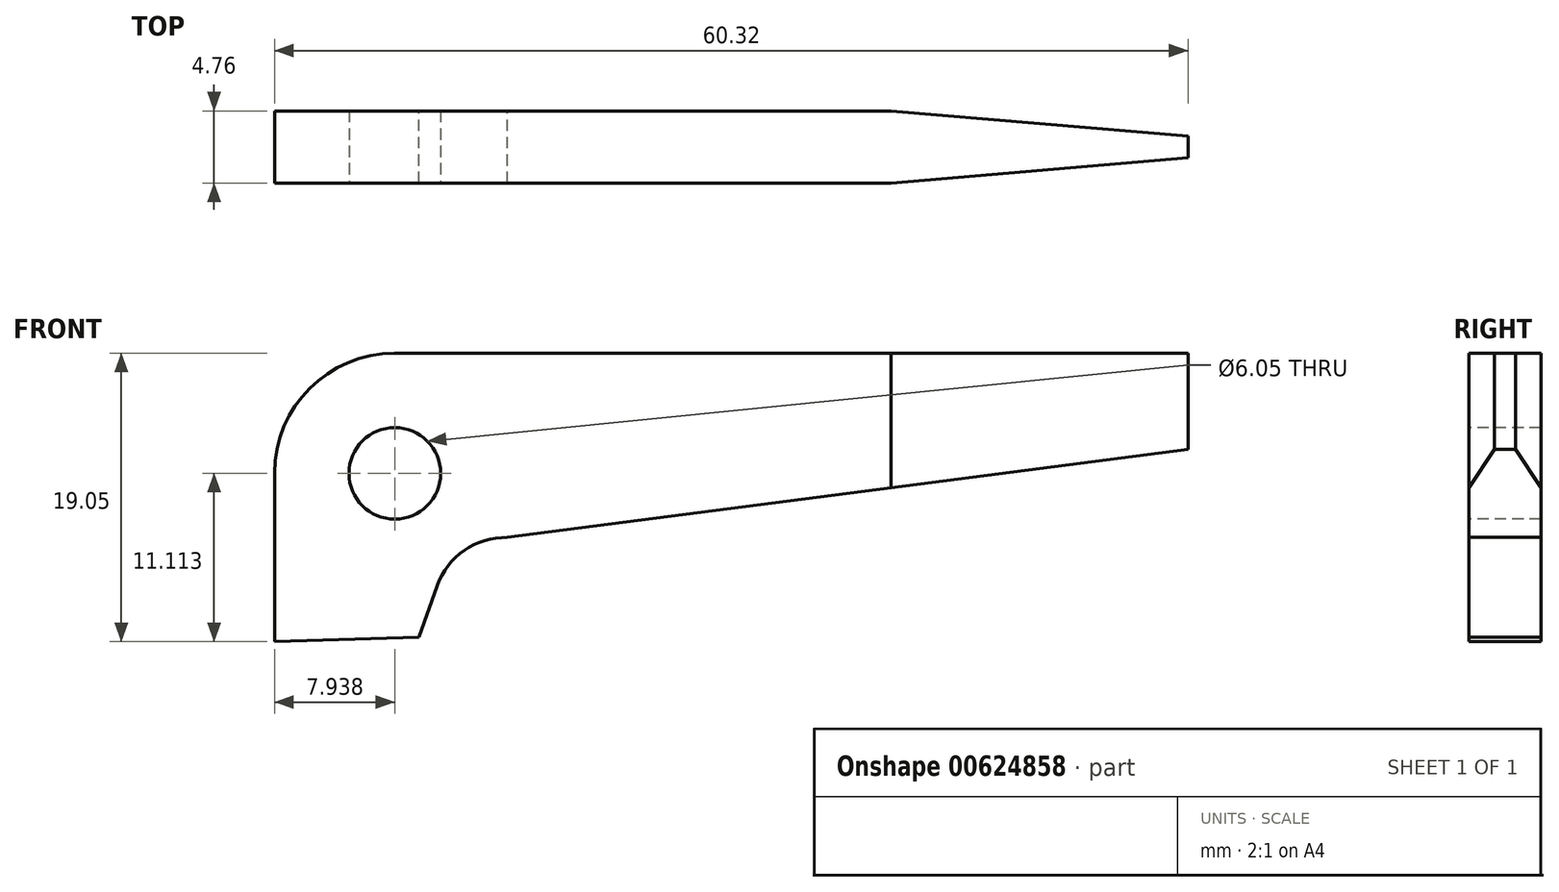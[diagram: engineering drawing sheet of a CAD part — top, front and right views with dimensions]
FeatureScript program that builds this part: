
annotation { "Feature Type Name" : "Feature", "Feature Type Description" : "" }
export const myFeature = defineFeature(function(context is Context, id is Id, definition is map)
    precondition{}
    {
        {
            var Q0;
            Q0=qCreatedBy(makeId("Front.planeOp"),FACE);
            var sketch = newSketch(context, id + "F0", { "sketchPlane" : qUnion([Q0])});
            skLineSegment(sketch, "E0.top", {"start": v(7.91, 19.05) * mm, "end": v(60.33, 19.05) * mm});
            skLineSegment(sketch, "E0.left", {"start": v(0, 0) * mm, "end": v(0, 11.14) * mm});
            skLineSegment(sketch, "E1", {"start": v(9.52, 0.28) * mm, "end": v(10.73, 3.69) * mm});
            skLineSegment(sketch, "E2", {"start": v(9.52, 0.28) * mm, "end": v(0, 0) * mm});
            skLineSegment(sketch, "E3", {"start": v(60.33, 12.7) * mm, "end": v(15.36, 6.88) * mm});
            skArc(sketch, "E4", {"start": v(15.36, 6.88) * mm, "mid": v(12.53, 6.03) * mm, "end": v(10.73, 3.69) * mm});
            skLineSegment(sketch, "E5", {"start": v(60.33, 19.05) * mm, "end": v(60.33, 12.7) * mm});
            skPoint(sketch, "E6.visualSharp", {"position": v(0, 19.05) * mm});
            skArc(sketch, "E6.filletArc", {"start": v(7.91, 19.05) * mm, "mid": v(2.32, 16.73) * mm, "end": v(0, 11.14) * mm});
            skSolve(sketch);
        }
        {
            var Q0;
            Q0=makeQuery(id+"F0.imprint","IMPRINT",FACE,{"disambiguationData":[TD([[makeQuery(id+"F0.imprint","IMPRINT",EDGE,{"derivedFrom":sQuery(id+"F0.wireOp",EDGE,"E0.top")}),-1.0]])]});
            extrude(context, id + "F1", {"entities" : qUnion([Q0]), "depth" : 4.76 * mm, "offsetDistance" : 25.4 * mm});
        }
        {
            var Q0;
            Q0=makeQuery(id+"F1.opExtrude","CAP_FACE",FACE,{"disambiguationData":[OSD([sQuery(id+"F0.wireOp",EDGE,"E0.top"),sQuery(id+"F0.wireOp",EDGE,"E0.left"),sQuery(id+"F0.wireOp",EDGE,"E1"),sQuery(id+"F0.wireOp",EDGE,"E2"),sQuery(id+"F0.wireOp",EDGE,"E3"),sQuery(id+"F0.wireOp",EDGE,"E4"),sQuery(id+"F0.wireOp",EDGE,"E5"),sQuery(id+"F0.wireOp",EDGE,"E6.filletArc")])],"isStart":false});
            var sketch = newSketch(context, id + "F2", { "sketchPlane" : qUnion([Q0])});
            skCircle(sketch, "E7", {"center": v(7.94, 11.11) * mm, "radius": 3.03 * mm});
            skSolve(sketch);
        }
        {
            var Q0;
            Q0=makeQuery(id+"F2.imprint","IMPRINT",FACE,{"disambiguationData":[TD([[makeQuery(id+"F2.imprint","IMPRINT",EDGE,{"derivedFrom":sQuery(id+"F2.wireOp",EDGE,"E7")}),1.0]])]});
            extrude(context, id + "F3", {"entities" : qUnion([Q0]), "operationType" : NewBodyOperationType.REMOVE, "oppositeDirection" : true, "depth" : 25.4 * mm, "offsetDistance" : 25.4 * mm});
        }
        {
            var Q0;
            Q0=makeQuery(id+"F1.opExtrude","SWEPT_FACE",FACE,{"disambiguationData":[OSD([sQuery(id+"F0.wireOp",EDGE,"E0.top")])]});
            var sketch = newSketch(context, id + "F4", { "sketchPlane" : qUnion([Q0])});
            skLineSegment(sketch, "E8", {"start": v(60.33, -1.67) * mm, "end": v(40.7, 0) * mm});
            skLineSegment(sketch, "E9", {"start": v(40.7, 0) * mm, "end": v(60.33, 0) * mm});
            skLineSegment(sketch, "E10", {"start": v(60.33, 0) * mm, "end": v(60.33, -1.67) * mm});
            skLineSegment(sketch, "E11", {"start": v(60.33, -2.38) * mm, "end": v(30.8, -2.38) * mm});
            skLineSegment(sketch, "E12.MirrorCS", {"start": v(60.33, -3.09) * mm, "end": v(40.7, -4.76) * mm});
            skLineSegment(sketch, "E13.MirrorCS", {"start": v(40.7, -4.76) * mm, "end": v(60.33, -4.76) * mm});
            skLineSegment(sketch, "E14.MirrorCS", {"start": v(60.33, -4.76) * mm, "end": v(60.33, -3.09) * mm});
            skSolve(sketch);
        }
        {
            var Q0;
            Q0 = qSketchRegion(id + "F4", true);
            extrude(context, id + "F5", {"entities" : qUnion([Q0]), "operationType" : NewBodyOperationType.REMOVE, "oppositeDirection" : true, "depth" : 25.4 * mm, "offsetDistance" : 25.4 * mm});
        }
    });
